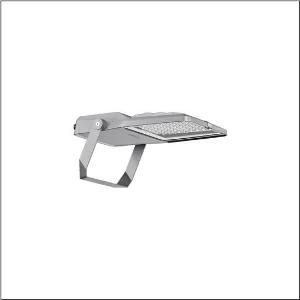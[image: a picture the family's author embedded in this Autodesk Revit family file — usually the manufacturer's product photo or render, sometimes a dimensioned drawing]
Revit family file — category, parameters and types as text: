
# Revit family: floodlight_fl_21_mini___pl43_5xa7776d2a1a_71d0
name_source: partatom
category: Lighting Fixtures
units: mm (PartAtom-declared; Revit-internal decimal feet)

## family parameters
Cut with Voids When Loaded = No
Host = Face
Light Source = No
Part Type = Normal
Room Calculation Point = No
Round Connector Dimension = Use Diameter
Shared = No

## types (1)
- --- (1 x LED, 18300 lm, 142.9 W, 3000K)
    Apparent Load = 143 VA
    CIE Flux Codes = 27 78 99 100 100
    Color Rendering = 70
    Color Temperature = 3000K
    Default Elevation = 1800 mm
    Description = Floodlight FL 21 mini, floodlight, primary light control with lens, of PMMA, primary optical cover: protective disc, of toughened safety glass, transparent, light distribution: PL43, light emission: direct distribution, installation type: surface-mounted, LED, High Power LED, rated luminous flux: 18.300lm, luminous efficacy: 128lm/W, light colour: 730, colour temperature: 3000K, control gear: Smart Interface (Zhaga), control: flexible luminous flux parameterisation, time-dependent luminous flux control, constant luminous flux control, overheat protection, pre-setting: logarithmic dimming characteristic, with terminal, 6-pole, mains connection: 220..240V, AC, 50/60Hz, start of lifetime: 143W, end of service life: 151W, reduction: 63W, luminaire housing, of diecast aluminium, powder-coated, SITECO metallic grey (DB 702S), corrosivity category C5 mid according to DIN EN ISO 12944, suitable for swimming pools, chlorine-resistant, sealing non-destructively replaceable, mounting bracket, of steel, galvanised, powder-coated, SITECO metallic grey (DB 702S), Smart Interface below and above, protection rating (complete): IP66, insulation class (complete): insulation class II (safety insulation), certification: CE, ENEC, VDE, protection symbol: D, impact resistance: IK08, permissible operating ambient temperature: -40..+40°C, permissible operating ambient temperature for outdoor applications: -40..+50°C, standard: DIN EN 12944, LABS conformity tested according to VDMA 24364:2018-05, packaging unit: 1 piece

Light Distribution: PL43
    Height = 70 mm
    Lamp = 1 x LED
    Lamp Light Flux = 18300 lm
    Lamp Power = 142.9 W
    Lamp count = 1
    Length = 485 mm
    Luminous efficacy = 128 lm/W
    Manufacturer = Siteco
    ModVariant = No
    Model = 5XA7776D2A1A
    Mounting Place = Pole
    Mounting Type = Pole annexe
    Number of Poles = 1
    OnlyDefault = Yes
    Power Factor = 1
    Product Name = Floodlight FL 21 mini | PL43
    Product group = floodlight | pylon annexe
    ProductGroupID = 6201
    Protection Class = Protection class II
    Protection Degree = IP 66
    RLX_Detail_Level = 1
    RLX_Emergency_Light_Flux = 0 lm
    RLX_Emergency_Type = 0
    RLX_Emergency_Type_DB = No
    RlxData = <blob elided: 96205 chars, md5=09e36349>
    Socket = socket
    Standby Power = 0 W
    System Light Flux = 18300 lm
    System Power = 143 W
    Type Comments = factory setting: luminous flux: 100 % | dim-lin: 254 | 730 mA
    Type Image = l_1006845.jpg
    URL = http://relux.com
    VarID = @adj_162033
    Voltage = 0 V
    Weight = 0.00 kg
    Width = 337 mm

## geometry (parser evidence)
native form markers: Blend x4, Sweep x13
no freeform markers — native parametric forms only
